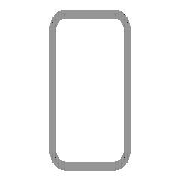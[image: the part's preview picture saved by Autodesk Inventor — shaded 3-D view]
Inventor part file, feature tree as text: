
AUTODESK INVENTOR PART (.ipt)
format: ipt  version: 2025 (Build 290162010, 162A)  size: 134,144 bytes
history: native  units: mm (DEFAULTED — no unit token found)
features: other x4, sketch x1, plane x1
ambient origin geometry x8: Origin, YZ Plane, XZ Plane, XY Plane, X Axis, Y Axis, Z Axis, Center Point
bodies: Solid1 (feature_tree), Body (feature_tree)
feature tree (6):
  parser-record x1  (decoder bookkeeping rows leaked as tree rows — omitted from the tree; the rows remain in map.json)
  other  "Driven Length"
  other  "Start Plane"
  other  "End Plane"
  sketch  "Sketch3"  dims[d3=2881.0mm d4=0.0mm d7=6.0mm d9=20.0mm d11=40.0mm d12=3.0mm d13=-0.0mm d14=2881.0mm d15=10.0mm d16=20.0mm d17=90.0deg d18=2881.0mm]
  plane  "Work Plane3"
